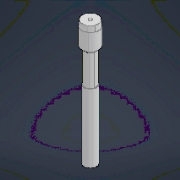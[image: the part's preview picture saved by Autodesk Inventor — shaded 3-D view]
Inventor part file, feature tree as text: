
AUTODESK INVENTOR PART (.ipt)
format: ipt  version: 2025.3 (Build 293356000, 356)  size: 148,480 bytes
history: native  units: mm
features: revolve x1, sketch x1
ambient origin geometry x8: Origin, YZ Plane, XZ Plane, XY Plane, X Axis, Y Axis, Z Axis, Center Point
bodies: Solid1 (feature_tree)
feature tree (2):
  revolve  "Revolution1"  [1 undecoded]
  sketch  "Sketch1"  dims[d1=45.0deg d2=0.872665mm d6=1.2mm d7=4.0mm d9=8.0mm d10=90.0deg d11=45.0deg]
note: 1 required parameter value undecoded (feature->parameter linkage not recoverable at this tier; creation-order binding heuristic only, values carry confidence <= 0.55)
